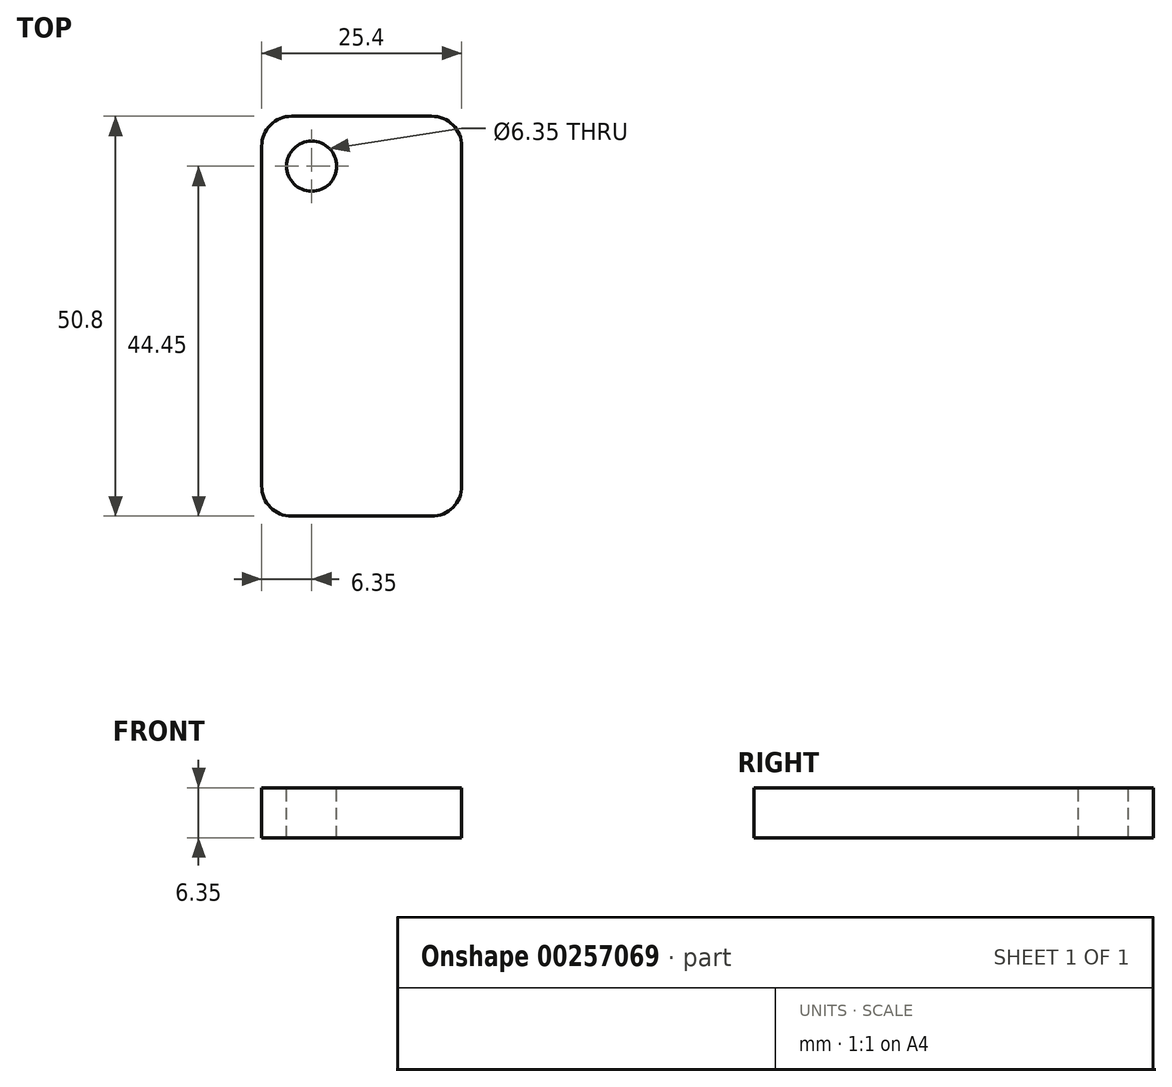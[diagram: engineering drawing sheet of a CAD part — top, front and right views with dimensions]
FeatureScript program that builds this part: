
annotation { "Feature Type Name" : "Feature", "Feature Type Description" : "" }
export const myFeature = defineFeature(function(context is Context, id is Id, definition is map)
    precondition{}
    {
        {
            var Q0;
            Q0=qCreatedBy(makeId("Top.planeOp"),FACE);
            var sketch = newSketch(context, id + "F0", { "sketchPlane" : qUnion([Q0])});
            skLineSegment(sketch, "E0.bottom", {"start": v(12.7, 25.4) * mm, "end": v(-12.7, 25.4) * mm});
            skLineSegment(sketch, "E0.top", {"start": v(12.7, -25.4) * mm, "end": v(-12.7, -25.4) * mm});
            skLineSegment(sketch, "E0.left", {"start": v(12.7, 25.4) * mm, "end": v(12.7, -25.4) * mm});
            skLineSegment(sketch, "E0.right", {"start": v(-12.7, 25.4) * mm, "end": v(-12.7, -25.4) * mm});
            skPoint(sketch, "E0.middle", {"position": v(0, 0) * mm});
            skSolve(sketch);
        }
        {
            var Q0;
            Q0 = qSketchRegion(id + "F0", true);
            extrude(context, id + "F1", {"entities" : qUnion([Q0]), "depth" : 6.35 * mm});
        }
        {
            var Q0;
            Q0=makeQuery(id+"F1.opExtrude","CAP_FACE",FACE,{"disambiguationData":[OSD([sQuery(id+"F0.wireOp",EDGE,"E0.bottom"),sQuery(id+"F0.wireOp",EDGE,"E0.top"),sQuery(id+"F0.wireOp",EDGE,"E0.left"),sQuery(id+"F0.wireOp",EDGE,"E0.right")])],"isStart":false});
            var sketch = newSketch(context, id + "F2", { "sketchPlane" : qUnion([Q0])});
            skCircle(sketch, "E1", {"center": v(-6.35, 19.05) * mm, "radius": 6.35 * mm, "construction": true});
            skCircle(sketch, "E2", {"center": v(-6.35, 19.05) * mm, "radius": 3.18 * mm});
            skSolve(sketch);
        }
        {
            var Q0;
            Q0=makeQuery(id+"F2.imprint","IMPRINT",FACE,{"disambiguationData":[TD([[makeQuery(id+"F2.imprint","IMPRINT",EDGE,{"derivedFrom":sQuery(id+"F2.wireOp",EDGE,"E2")}),1.0]])]});
            extrude(context, id + "F3", {"entities" : qUnion([Q0]), "operationType" : NewBodyOperationType.REMOVE, "oppositeDirection" : true, "depth" : 25.4 * mm});
        }
        {
            var Q0;
            Q0=makeQuery(id+"F1.opExtrude","SWEPT_EDGE",EDGE,{"disambiguationData":[OSD([sQuery(id+"F0.wireOp",EDGE,"E0.bottom"),sQuery(id+"F0.wireOp",EDGE,"E0.right")])]});
            var Q1;
            Q1=makeQuery(id+"F1.opExtrude","SWEPT_EDGE",EDGE,{"disambiguationData":[OSD([sQuery(id+"F0.wireOp",EDGE,"E0.bottom"),sQuery(id+"F0.wireOp",EDGE,"E0.left")])]});
            var Q2;
            Q2=makeQuery(id+"F1.opExtrude","SWEPT_EDGE",EDGE,{"disambiguationData":[OSD([sQuery(id+"F0.wireOp",EDGE,"E0.top"),sQuery(id+"F0.wireOp",EDGE,"E0.right")])]});
            var Q3;
            Q3=makeQuery(id+"F1.opExtrude","SWEPT_EDGE",EDGE,{"disambiguationData":[OSD([sQuery(id+"F0.wireOp",EDGE,"E0.top"),sQuery(id+"F0.wireOp",EDGE,"E0.left")])]});
            fillet(context, id + "F4", {"entities" : qUnion([Q0, Q1, Q2, Q3]), "radius" : 3.8 * mm, "tangentPropagation" : true, "allowEdgeOverflow" : false});
        }
    });
